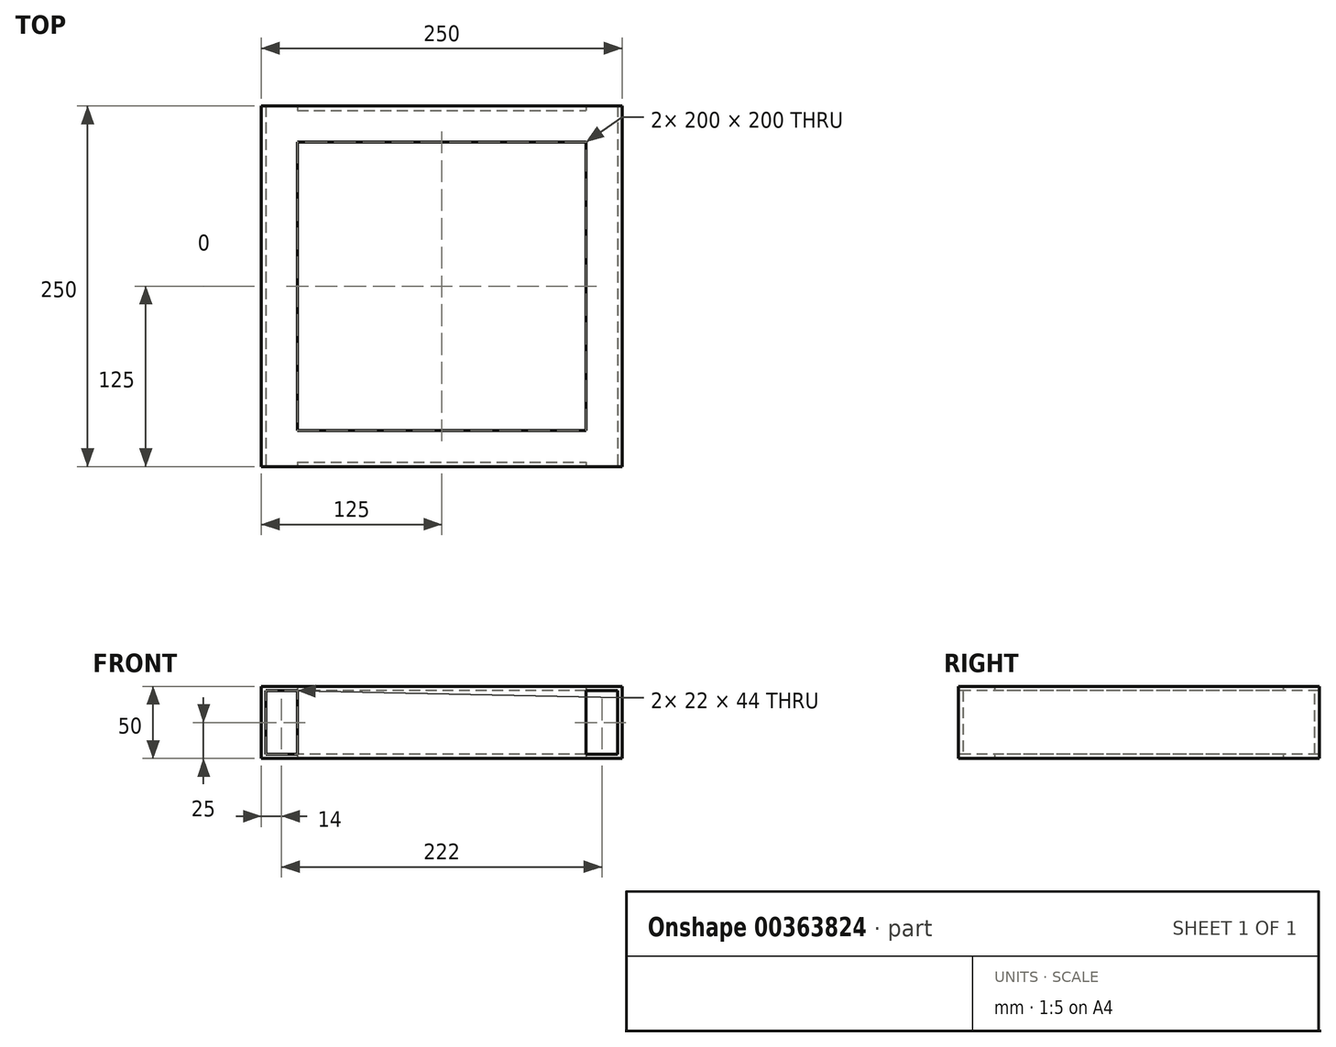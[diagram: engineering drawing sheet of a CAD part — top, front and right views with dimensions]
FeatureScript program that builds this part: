
annotation { "Feature Type Name" : "Feature", "Feature Type Description" : "" }
export const myFeature = defineFeature(function(context is Context, id is Id, definition is map)
    precondition{}
    {
        {
            var Q0;
            Q0=qCreatedBy(makeId("Top.planeOp"),FACE);
            var sketch = newSketch(context, id + "F0", { "sketchPlane" : qUnion([Q0])});
            skLineSegment(sketch, "E0.bottom", {"start": v(125, 125) * mm, "end": v(-125, 125) * mm});
            skLineSegment(sketch, "E0.top", {"start": v(125, -125) * mm, "end": v(-125, -125) * mm});
            skLineSegment(sketch, "E0.left", {"start": v(125, 125) * mm, "end": v(125, -125) * mm});
            skLineSegment(sketch, "E0.right", {"start": v(-125, 125) * mm, "end": v(-125, -125) * mm});
            skPoint(sketch, "E0.middle", {"position": v(0, 0) * mm});
            skLineSegment(sketch, "E1.bottom", {"start": v(100, 100) * mm, "end": v(-100, 100) * mm});
            skLineSegment(sketch, "E1.top", {"start": v(100, -100) * mm, "end": v(-100, -100) * mm});
            skLineSegment(sketch, "E1.left", {"start": v(100, 100) * mm, "end": v(100, -100) * mm});
            skLineSegment(sketch, "E1.right", {"start": v(-100, 100) * mm, "end": v(-100, -100) * mm});
            skLineSegment(sketch, "E2", {"start": v(-100, 27.52) * mm, "end": v(-125, 27.52) * mm, "construction": true});
            skLineSegment(sketch, "E3", {"start": v(-28.39, 100) * mm, "end": v(-28.39, 125) * mm, "construction": true});
            skLineSegment(sketch, "E4", {"start": v(31.1, -100) * mm, "end": v(31.1, -125) * mm, "construction": true});
            skLineSegment(sketch, "E5", {"start": v(100, -21.97) * mm, "end": v(125, -21.97) * mm, "construction": true});
            skSolve(sketch);
        }
        {
            var Q0;
            Q0=makeQuery(id+"F0.imprint","IMPRINT",FACE,{"disambiguationData":[TD([[makeQuery(id+"F0.imprint","IMPRINT",EDGE,{"derivedFrom":sQuery(id+"F0.wireOp",EDGE,"E0.bottom")}),1.0]])]});
            extrude(context, id + "F1", {"entities" : qUnion([Q0]), "depth" : 50 * mm});
        }
        {
            var Q0;
            Q0=makeQuery(id+"F1.opExtrude","SWEPT_FACE",FACE,{"disambiguationData":[OSD([sQuery(id+"F0.wireOp",EDGE,"E0.top")])]});
            var sketch = newSketch(context, id + "F2", { "sketchPlane" : qUnion([Q0])});
            skLineSegment(sketch, "E6.bottom", {"start": v(122, 47) * mm, "end": v(100, 47) * mm});
            skLineSegment(sketch, "E6.top", {"start": v(122, 3) * mm, "end": v(100, 3) * mm});
            skLineSegment(sketch, "E6.left", {"start": v(122, 47) * mm, "end": v(122, 3) * mm});
            skLineSegment(sketch, "E6.right", {"start": v(100, 47) * mm, "end": v(100, 3) * mm});
            skLineSegment(sketch, "E7", {"start": v(41.54, 47) * mm, "end": v(41.54, 50) * mm, "construction": true});
            skLineSegment(sketch, "E8", {"start": v(122, 32.59) * mm, "end": v(125, 32.59) * mm, "construction": true});
            skLineSegment(sketch, "E9", {"start": v(42.22, 3) * mm, "end": v(42.22, 0) * mm, "construction": true});
            skLineSegment(sketch, "E10.MirrorCS", {"start": v(-100, 47) * mm, "end": v(-100, 3) * mm});
            skLineSegment(sketch, "E11.MirrorCS", {"start": v(-122, 3) * mm, "end": v(-100, 3) * mm});
            skLineSegment(sketch, "E12.MirrorCS", {"start": v(-122, 47) * mm, "end": v(-122, 3) * mm});
            skLineSegment(sketch, "E13.MirrorCS", {"start": v(-122, 47) * mm, "end": v(-100, 47) * mm});
            skSolve(sketch);
        }
        {
            var Q0;
            Q0=makeQuery(id+"F2.imprint","IMPRINT",FACE,{"disambiguationData":[TD([[makeQuery(id+"F2.imprint","IMPRINT",EDGE,{"derivedFrom":sQuery(id+"F2.wireOp",EDGE,"E10.MirrorCS")}),-1.0]])]});
            var Q1;
            Q1=makeQuery(id+"F2.imprint","IMPRINT",FACE,{"disambiguationData":[TD([[makeQuery(id+"F2.imprint","IMPRINT",EDGE,{"derivedFrom":sQuery(id+"F2.wireOp",EDGE,"E6.bottom")}),1.0]])]});
            var Q2;
            Q2=makeQuery(id+"F1.opExtrude","SWEPT_FACE",FACE,{"disambiguationData":[OSD([sQuery(id+"F0.wireOp",EDGE,"E0.bottom")])]});
            extrude(context, id + "F3", {"entities" : qUnion([Q0, Q1]), "operationType" : NewBodyOperationType.REMOVE, "endBound" : BoundingType.UP_TO_SURFACE, "oppositeDirection" : true, "endBoundEntityFace" : qUnion([Q2]), "depth" : 25 * mm});
        }
        {
            var Q0;
            Q0=qCreatedBy(makeId("Right.planeOp"),FACE);
            var sketch = newSketch(context, id + "F4", { "sketchPlane" : qUnion([Q0])});
            skLineSegment(sketch, "E14.bottom", {"start": v(-47.31, 47) * mm, "end": v(-22.31, 47) * mm});
            skLineSegment(sketch, "E14.top", {"start": v(-47.31, 3) * mm, "end": v(-22.31, 3) * mm});
            skLineSegment(sketch, "E14.left", {"start": v(-47.31, 47) * mm, "end": v(-47.31, 3) * mm});
            skLineSegment(sketch, "E14.right", {"start": v(-22.31, 47) * mm, "end": v(-22.31, 3) * mm});
            skLineSegment(sketch, "E15", {"start": v(-47.31, 33.81) * mm, "end": v(-50.31, 33.81) * mm, "construction": true});
            skLineSegment(sketch, "E16", {"start": v(-34.81, 3) * mm, "end": v(-34.81, 0) * mm, "construction": true});
            skLineSegment(sketch, "E17", {"start": v(-36.14, 47) * mm, "end": v(-36.14, 50) * mm, "construction": true});
            skLineSegment(sketch, "E18.MirrorCS", {"start": v(47.31, 47) * mm, "end": v(22.31, 47) * mm});
            skLineSegment(sketch, "E19.MirrorCS", {"start": v(22.31, 47) * mm, "end": v(22.31, 3) * mm});
            skLineSegment(sketch, "E20.MirrorCS", {"start": v(47.31, 47) * mm, "end": v(47.31, 3) * mm});
            skLineSegment(sketch, "E21.MirrorCS", {"start": v(47.31, 3) * mm, "end": v(22.31, 3) * mm});
            skSolve(sketch);
        }
        {
            var Q0;
            Q0 = qSketchRegion(id + "F4", true);
            var Q1;
            Q1=makeQuery(id+"F1.opExtrude","SWEPT_FACE",FACE,{"disambiguationData":[OSD([sQuery(id+"F0.wireOp",EDGE,"E0.left")])]});
            extrude(context, id + "F5", {"entities" : qUnion([Q0]), "operationType" : NewBodyOperationType.REMOVE, "endBound" : BoundingType.UP_TO_SURFACE, "endBoundEntityFace" : qUnion([Q1]), "depth" : 25 * mm});
        }
        {
            var Q0;
            Q0=qCreatedBy(makeId("Right.planeOp"),FACE);
            var sketch = newSketch(context, id + "F6", { "sketchPlane" : qUnion([Q0])});
            skLineSegment(sketch, "E22.bottom", {"start": v(122, 47) * mm, "end": v(97, 47) * mm});
            skLineSegment(sketch, "E22.top", {"start": v(122, 3) * mm, "end": v(97, 3) * mm});
            skLineSegment(sketch, "E22.left", {"start": v(122, 47) * mm, "end": v(122, 3) * mm});
            skLineSegment(sketch, "E22.right", {"start": v(97, 47) * mm, "end": v(97, 3) * mm});
            skLineSegment(sketch, "E23", {"start": v(37.61, 47) * mm, "end": v(37.61, 50) * mm, "construction": true});
            skLineSegment(sketch, "E24", {"start": v(122, 26.86) * mm, "end": v(125, 26.86) * mm, "construction": true});
            skLineSegment(sketch, "E25", {"start": v(109.5, 3) * mm, "end": v(109.5, 0) * mm, "construction": true});
            skLineSegment(sketch, "E26.MirrorCS", {"start": v(-122, 47) * mm, "end": v(-97, 47) * mm});
            skLineSegment(sketch, "E27.MirrorCS", {"start": v(-122, 47) * mm, "end": v(-122, 3) * mm});
            skLineSegment(sketch, "E28.MirrorCS", {"start": v(-97, 47) * mm, "end": v(-97, 3) * mm});
            skLineSegment(sketch, "E29.MirrorCS", {"start": v(-122, 3) * mm, "end": v(-97, 3) * mm});
            skSolve(sketch);
        }
        {
            var Q0;
            Q0 = qSketchRegion(id + "F6", true);
            var Q1;
            Q1=makeQuery(id+"F1.opExtrude","SWEPT_FACE",FACE,{"disambiguationData":[OSD([sQuery(id+"F0.wireOp",EDGE,"E0.right")])]});
            extrude(context, id + "F7", {"entities" : qUnion([Q0]), "operationType" : NewBodyOperationType.REMOVE, "endBound" : BoundingType.UP_TO_SURFACE, "oppositeDirection" : true, "endBoundEntityFace" : qUnion([Q1]), "depth" : 25 * mm});
        }
        {
            var Q0;
            Q0=makeQuery(id+"F7.boolean.opBoolean","COPY",FACE,{"derivedFrom":makeQuery(id+"F7.opExtrude","SWEPT_FACE",FACE,{"disambiguationData":[OSD([sQuery(id+"F6.wireOp",EDGE,"E22.right")])]})});
            extrude(context, id + "F8", {"entities" : qUnion([Q0]), "operationType" : NewBodyOperationType.ADD, "depth" : 25 * mm});
        }
        {
            var Q0;
            Q0=makeQuery(id+"F7.boolean.opBoolean","COPY",FACE,{"disambiguationData":[TD([makeQuery(id+"F1.opExtrude","SWEPT_FACE",FACE,{"disambiguationData":[OSD([sQuery(id+"F0.wireOp",EDGE,"E0.right")])]})])],"derivedFrom":makeQuery(id+"F7.opExtrude","SWEPT_FACE",FACE,{"disambiguationData":[OSD([sQuery(id+"F6.wireOp",EDGE,"E27.MirrorCS")])]})});
            extrude(context, id + "F9", {"entities" : qUnion([Q0]), "operationType" : NewBodyOperationType.ADD, "depth" : 25 * mm});
        }
        {
            var Q0;
            Q0=makeQuery(id+"F5.boolean.opBoolean","COPY",FACE,{"disambiguationData":[TD([makeQuery(id+"F1.opExtrude","SWEPT_FACE",FACE,{"disambiguationData":[OSD([sQuery(id+"F0.wireOp",EDGE,"E0.left")])]})])],"derivedFrom":makeQuery(id+"F5.opExtrude","SWEPT_FACE",FACE,{"disambiguationData":[OSD([sQuery(id+"F4.wireOp",EDGE,"E14.left")])]})});
            extrude(context, id + "F10", {"entities" : qUnion([Q0]), "operationType" : NewBodyOperationType.ADD, "depth" : 25 * mm});
        }
        {
            var Q0;
            Q0=makeQuery(id+"F5.boolean.opBoolean","COPY",FACE,{"derivedFrom":makeQuery(id+"F5.opExtrude","SWEPT_FACE",FACE,{"disambiguationData":[OSD([sQuery(id+"F4.wireOp",EDGE,"E19.MirrorCS")])]})});
            extrude(context, id + "F11", {"entities" : qUnion([Q0]), "operationType" : NewBodyOperationType.ADD, "depth" : 25 * mm});
        }
        {
            var Q0;
            Q0=makeQuery(id+"F7.boolean.opBoolean","COPY",FACE,{"derivedFrom":makeQuery(id+"F7.opExtrude","CAP_FACE",FACE,{"disambiguationData":[OSD([sQuery(id+"F6.wireOp",EDGE,"E26.MirrorCS"),sQuery(id+"F6.wireOp",EDGE,"E27.MirrorCS"),sQuery(id+"F6.wireOp",EDGE,"E28.MirrorCS"),sQuery(id+"F6.wireOp",EDGE,"E29.MirrorCS")])],"isStart":true})});
            var Q1;
            {var subQ0=sQuery(id+"F0.wireOp",EDGE,"E0.left");Q1=makeQuery(id+"F11.boolean.opBoolean","MERGE",FACE,{"derivedFrom":[makeQuery(id+"F10.boolean.opBoolean","MERGE",FACE,{"derivedFrom":[makeQuery(id+"F1.opExtrude","SWEPT_FACE",FACE,{"disambiguationData":[OSD([subQ0])]}),makeQuery(id+"F10.opExtrude","SWEPT_FACE",FACE,{"disambiguationData":[OSD([subQ0,sQuery(id+"F4.wireOp",EDGE,"E14.left")])]})]}),makeQuery(id+"F11.opExtrude","SWEPT_FACE",FACE,{"disambiguationData":[OSD([subQ0,sQuery(id+"F4.wireOp",EDGE,"E19.MirrorCS")])]})]});}
            extrude(context, id + "F12", {"entities" : qUnion([Q0]), "operationType" : NewBodyOperationType.REMOVE, "endBound" : BoundingType.UP_TO_SURFACE, "oppositeDirection" : true, "endBoundEntityFace" : qUnion([Q1]), "depth" : 25 * mm});
        }
        {
            var Q0;
            Q0=makeQuery(id+"F7.boolean.opBoolean","COPY",FACE,{"derivedFrom":makeQuery(id+"F7.opExtrude","CAP_FACE",FACE,{"disambiguationData":[OSD([sQuery(id+"F6.wireOp",EDGE,"E22.bottom"),sQuery(id+"F6.wireOp",EDGE,"E22.top"),sQuery(id+"F6.wireOp",EDGE,"E22.left"),sQuery(id+"F6.wireOp",EDGE,"E22.right")])],"isStart":true})});
            var Q1;
            {var subQ0=sQuery(id+"F0.wireOp",EDGE,"E0.left");Q1=makeQuery(id+"F11.boolean.opBoolean","MERGE",FACE,{"derivedFrom":[makeQuery(id+"F10.boolean.opBoolean","MERGE",FACE,{"derivedFrom":[makeQuery(id+"F1.opExtrude","SWEPT_FACE",FACE,{"disambiguationData":[OSD([subQ0])]}),makeQuery(id+"F10.opExtrude","SWEPT_FACE",FACE,{"disambiguationData":[OSD([subQ0,sQuery(id+"F4.wireOp",EDGE,"E14.left")])]})]}),makeQuery(id+"F11.opExtrude","SWEPT_FACE",FACE,{"disambiguationData":[OSD([subQ0,sQuery(id+"F4.wireOp",EDGE,"E19.MirrorCS")])]})]});}
            extrude(context, id + "F13", {"entities" : qUnion([Q0]), "operationType" : NewBodyOperationType.REMOVE, "endBound" : BoundingType.UP_TO_SURFACE, "oppositeDirection" : true, "endBoundEntityFace" : qUnion([Q1]), "depth" : 25 * mm});
        }
        {
            var Q0;
            Q0=makeQuery(id+"F13.boolean.opBoolean","COPY",FACE,{"derivedFrom":makeQuery(id+"F13.opExtrude","SWEPT_FACE",FACE,{"disambiguationData":[OSD([sQuery(id+"F0.wireOp",EDGE,"E1.bottom"),sQuery(id+"F6.wireOp",EDGE,"E22.bottom"),sQuery(id+"F6.wireOp",EDGE,"E22.top"),sQuery(id+"F6.wireOp",EDGE,"E22.left"),sQuery(id+"F6.wireOp",EDGE,"E22.right")])]})});
            extrude(context, id + "F14", {"entities" : qUnion([Q0]), "operationType" : NewBodyOperationType.ADD, "depth" : 25 * mm});
        }
        {
            var Q0;
            Q0=makeQuery(id+"F12.boolean.opBoolean","COPY",FACE,{"derivedFrom":makeQuery(id+"F12.opExtrude","SWEPT_FACE",FACE,{"disambiguationData":[OSD([sQuery(id+"F6.wireOp",EDGE,"E27.MirrorCS")])]})});
            extrude(context, id + "F15", {"entities" : qUnion([Q0]), "operationType" : NewBodyOperationType.ADD, "depth" : 25 * mm});
        }
    });
